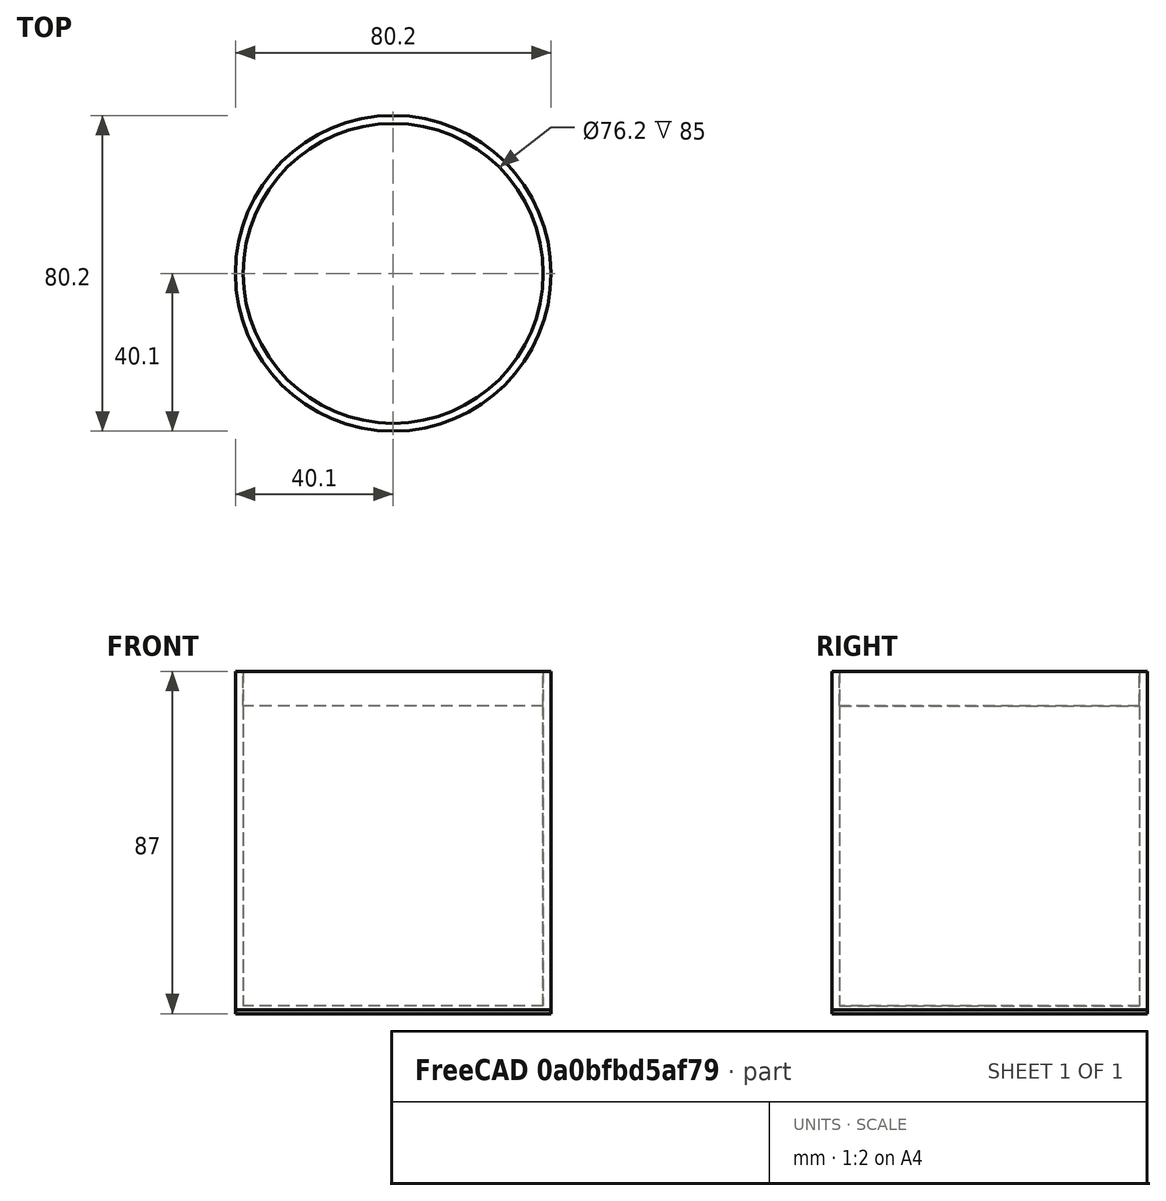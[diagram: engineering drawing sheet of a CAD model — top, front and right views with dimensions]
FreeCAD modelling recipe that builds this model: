
FCSTD DOCUMENT  (FreeCAD 1.0R39319 (Git))
Label: LezioneCAD
License: All rights reserved
LicenseURL: https://en.wikipedia.org/wiki/All_rights_reserved
objects: Sketcher::SketchObject×4, PartDesign::Body×4, PartDesign::Revolution×3, PartDesign::Pad×1, Mesh::Feature×1
note: 24 computed .brp shape members not serialized (recipe doc carries the construction recipe); baked Part::Feature solids carry a one-line shape summary decoded from their .brp

FEATURE [Sketcher::SketchObject] Sketch
  ArcFitTolerance = 1e-06
  AttachmentSupport = -> [XY_Plane]
  FullyConstrained = true
  MakeInternals = false
  MapMode = 5
  sketch-geometry (1):
    g0: Circle CenterX=0 CenterY=0 CenterZ=0 NormalX=0 NormalY=0 NormalZ=1 AngleXU=0 Radius=38.1
  constraints (2):
    c: Coincident(g0,g-1)
    c: Diameter(g0) = 76.2
FEATURE [PartDesign::Pad] Pad
  Direction = (0,0,1)
  Length = 76.2
  Length2 = 10
  Profile = -> Sketch
  ReferenceAxis = -> Sketch [N_Axis]
  Refine = true
  Suppressed = false
  Type = 0
FEATURE [PartDesign::Body] Body  label="LaBr3"
  AllowCompound = false
  Group = -> [Sketch,Pad]
  Origin = -> Origin
  Tip = -> Pad
FEATURE [Sketcher::SketchObject] Sketch001
  ArcFitTolerance = 1e-06
  AttachmentSupport = -> [XZ_Plane001]
  FullyConstrained = true
  MakeInternals = false
  MapMode = 5
  Placement = pos=(0,0,0) rot=(1,0,0;1.5708rad)
  sketch-geometry (6):
    g0: LineSegment StartX=0 StartY=0 StartZ=0 EndX=0 EndY=-2 EndZ=0
    g1: LineSegment StartX=0 StartY=-2 StartZ=0 EndX=40.1 EndY=-2 EndZ=0
    g2: LineSegment StartX=40.1 StartY=-2 StartZ=0 EndX=40.1 EndY=85 EndZ=0
    g3: LineSegment StartX=40.1 StartY=85 StartZ=0 EndX=38.1 EndY=85 EndZ=0
    g4: LineSegment StartX=38.1 StartY=85 StartZ=0 EndX=38.1 EndY=0 EndZ=0
    g5: LineSegment StartX=38.1 StartY=0 StartZ=0 EndX=0 EndY=0 EndZ=0
  constraints (17):
    c: Vertical(g0)
    c: Coincident(g0,g1)
    c: Horizontal(g1)
    c: Coincident(g1,g2)
    c: Vertical(g2)
    c: Coincident(g2,g3)
    c: Horizontal(g3)
    c: Coincident(g3,g4)
    c: Vertical(g4)
    c: Coincident(g4,g5)
    c: Coincident(g5,g0)
    c: Horizontal(g5)
    c: Distance(g-2,g4) = 38.1
    c: Distance(g-1,g3) = 85
    c: Distance(g2,g4) = 2
    c: Distance(g5,g1) = 2
    c: Coincident(g0,g-1)
FEATURE [PartDesign::Revolution] Revolution
  Angle = 360
  Angle2 = 60
  Axis = (0,2e-16,1)
  Base = (0,0,0)
  Placement = pos=(0,0,0) rot=(1,0,0;1.5708rad)
  Profile = -> Sketch001
  ReferenceAxis = -> Sketch001 [V_Axis]
  Refine = true
  Reversed = true
  Suppressed = false
  Type = 0
FEATURE [PartDesign::Body] Body001  label="Reflector"
  AllowCompound = false
  Group = -> [Sketch001,Revolution]
  Origin = -> Origin001
  Tip = -> Revolution
FEATURE [Sketcher::SketchObject] Sketch003
  ArcFitTolerance = 1e-06
  AttachmentSupport = -> [XZ_Plane002]
  FullyConstrained = true
  MakeInternals = false
  MapMode = 5
  Placement = pos=(0,0,0) rot=(1,0,0;1.5708rad)
  sketch-geometry (4):
    g0: LineSegment StartX=0 StartY=85 StartZ=0 EndX=0 EndY=76.2 EndZ=0
    g1: LineSegment StartX=0 StartY=76.2 StartZ=0 EndX=38.1 EndY=76.2 EndZ=0
    g2: LineSegment StartX=38.1 StartY=76.2 StartZ=0 EndX=38.1 EndY=85 EndZ=0
    g3: LineSegment StartX=38.1 StartY=85 StartZ=0 EndX=0 EndY=85 EndZ=0
  constraints (12):
    c: Coincident(g0,g1)
    c: Coincident(g1,g2)
    c: Coincident(g2,g3)
    c: Coincident(g3,g0)
    c: Vertical(g0)
    c: Vertical(g2)
    c: Horizontal(g1)
    c: Horizontal(g3)
    c: PointOnObject(g0,g-2)
    c: Distance(g2,g0) = 38.1
    c: Distance(g3,g1) = 8.8
    c: Distance(g0,g-1) = 76.2
FEATURE [PartDesign::Revolution] Revolution001
  Angle = 360
  Angle2 = 60
  Axis = (0,2e-16,1)
  Base = (0,0,0)
  Placement = pos=(0,0,0) rot=(1,0,0;1.5708rad)
  Profile = -> Sketch003
  ReferenceAxis = -> Sketch003 [V_Axis]
  Refine = true
  Reversed = true
  Suppressed = false
  Type = 0
FEATURE [PartDesign::Body] Body002  label="Window"
  AllowCompound = false
  Group = -> [Sketch003,Revolution001]
  Origin = -> Origin002
  Tip = -> Revolution001
FEATURE [Sketcher::SketchObject] Sketch004
  ArcFitTolerance = 1e-06
  AttachmentSupport = -> [YZ_Plane003]
  FullyConstrained = true
  MakeInternals = false
  MapMode = 5
  Placement = pos=(0,0,0) rot=(0.57735,0.57735,0.57735;2.0944rad)
  sketch-geometry (6):
    g0: LineSegment StartX=0 StartY=-2 StartZ=0 EndX=0 EndY=-1 EndZ=0
    g1: LineSegment StartX=0 StartY=-1 StartZ=0 EndX=41.1 EndY=-1 EndZ=0
    g2: LineSegment StartX=41.1 StartY=-1 StartZ=0 EndX=41.1 EndY=86 EndZ=0
    g3: LineSegment StartX=41.1 StartY=86 StartZ=0 EndX=40.1 EndY=86 EndZ=0
    g4: LineSegment StartX=40.1 StartY=86 StartZ=0 EndX=40.1 EndY=-2 EndZ=0
    g5: LineSegment StartX=40.1 StartY=-2 StartZ=0 EndX=0 EndY=-2 EndZ=0
  constraints (18):
    c: Coincident(g0,g1)
    c: Horizontal(g1)
    c: Coincident(g1,g2)
    c: Vertical(g2)
    c: Coincident(g2,g3)
    c: Horizontal(g3)
    c: Coincident(g3,g4)
    c: Vertical(g4)
    c: Coincident(g4,g5)
    c: Coincident(g5,g0)
    c: Horizontal(g5)
    c: PointOnObject(g0,g-2)
    c: PointOnObject(g0,g-2)
    c: Distance(g-1,g5) = 2
    c: Distance(g-2,g4) = 40.1
    c: Distance(g1,g5) = 1
    c: Distance(g2,g4) = 1
    c: DistanceY(g1,g2) = 87
FEATURE [PartDesign::Revolution] Revolution002
  Angle = 360
  Angle2 = 60
  Axis = (0,0,1)
  Base = (0,0,0)
  Placement = pos=(0,0,0) rot=(1,1,1;2.0944rad)
  Profile = -> Sketch004
  ReferenceAxis = -> Sketch004 [V_Axis]
  Refine = true
  Reversed = true
  Suppressed = false
  Type = 0
FEATURE [PartDesign::Body] Body003  label="Shell"
  AllowCompound = false
  Group = -> [Sketch004,Revolution002]
  Origin = -> Origin003
  Tip = -> Revolution002
FEATURE [Mesh::Feature] Mesh  label="LaBr3 (Meshed)"
